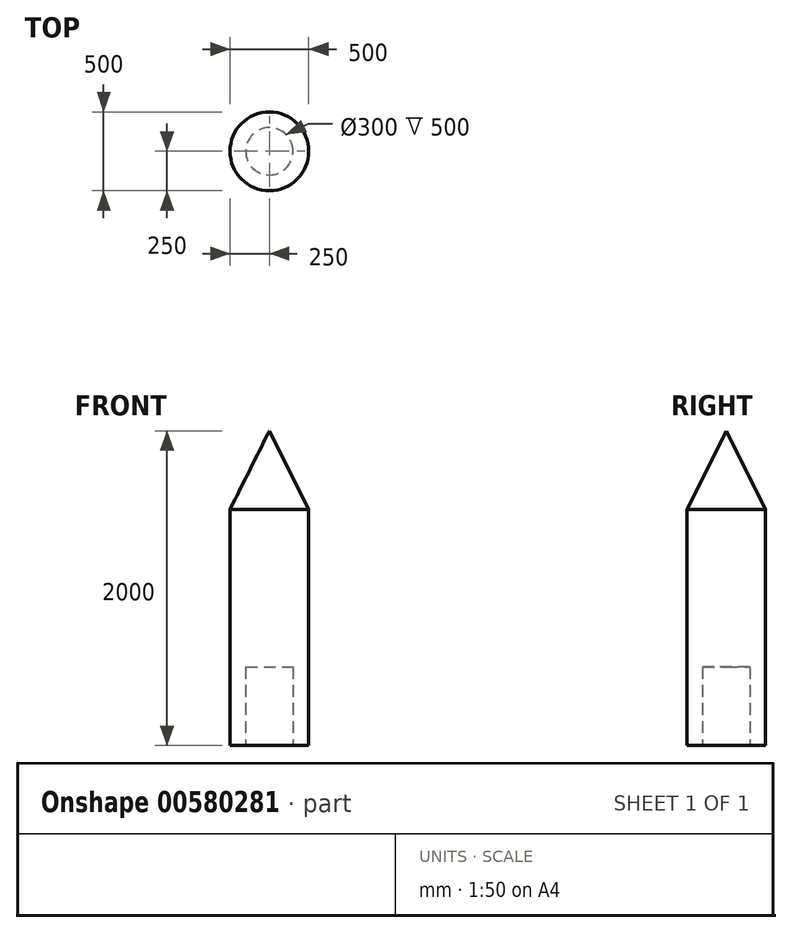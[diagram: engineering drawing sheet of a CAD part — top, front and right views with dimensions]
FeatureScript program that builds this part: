
annotation { "Feature Type Name" : "Feature", "Feature Type Description" : "" }
export const myFeature = defineFeature(function(context is Context, id is Id, definition is map)
    precondition{}
    {
        {
            var Q0;
            Q0=qCreatedBy(makeId("Top.planeOp"),FACE);
            var sketch = newSketch(context, id + "F0", { "sketchPlane" : qUnion([Q0])});
            skCircle(sketch, "E0", {"center": v(0, 0) * mm, "radius": 250 * mm});
            skSolve(sketch);
        }
        {
            var Q0;
            Q0 = qSketchRegion(id + "F0", true);
            extrude(context, id + "F1", {"entities" : qUnion([Q0]), "depth" : 1500 * mm, "offsetDistance" : 25 * mm});
        }
        {
            var Q0;
            Q0=qCreatedBy(makeId("Front.planeOp"),FACE);
            var sketch = newSketch(context, id + "F2", { "sketchPlane" : qUnion([Q0])});
            skLineSegment(sketch, "E1", {"start": v(0, 1500) * mm, "end": v(0, 2000) * mm});
            skLineSegment(sketch, "E2", {"start": v(0, 2000) * mm, "end": v(250, 1500) * mm});
            skLineSegment(sketch, "E3", {"start": v(0, 1500) * mm, "end": v(250, 1500) * mm});
            skSolve(sketch);
        }
        {
            var Q0;
            Q0=makeQuery(id+"F2.imprint","IMPRINT",FACE,{"disambiguationData":[TD([[makeQuery(id+"F2.imprint","IMPRINT",EDGE,{"derivedFrom":sQuery(id+"F2.wireOp",EDGE,"E1")}),-1.0]])]});
            var Q1;
            Q1=sQuery(id+"F2.wireOp",EDGE,"E1");
            revolve(context, id + "F3", {"operationType" : NewBodyOperationType.ADD, "entities" : qUnion([Q0]), "axis" : qUnion([Q1]), "revolveType" : RevolveType.FULL});
        }
        {
            var Q0;
            Q0=makeQuery(id+"F1.opExtrude","CAP_FACE",FACE,{"disambiguationData":[OSD([sQuery(id+"F0.wireOp",EDGE,"E0")])],"isStart":true});
            var sketch = newSketch(context, id + "F4", { "sketchPlane" : qUnion([Q0])});
            skCircle(sketch, "E4", {"center": v(0, 0) * mm, "radius": 150 * mm});
            skSolve(sketch);
        }
        {
            var Q0;
            Q0=makeQuery(id+"F4.imprint","IMPRINT",FACE,{"disambiguationData":[TD([[makeQuery(id+"F4.imprint","IMPRINT",EDGE,{"derivedFrom":sQuery(id+"F4.wireOp",EDGE,"E4")}),1.0]])]});
            extrude(context, id + "F5", {"entities" : qUnion([Q0]), "operationType" : NewBodyOperationType.REMOVE, "oppositeDirection" : true, "depth" : 500 * mm, "offsetDistance" : 25 * mm});
        }
    });
